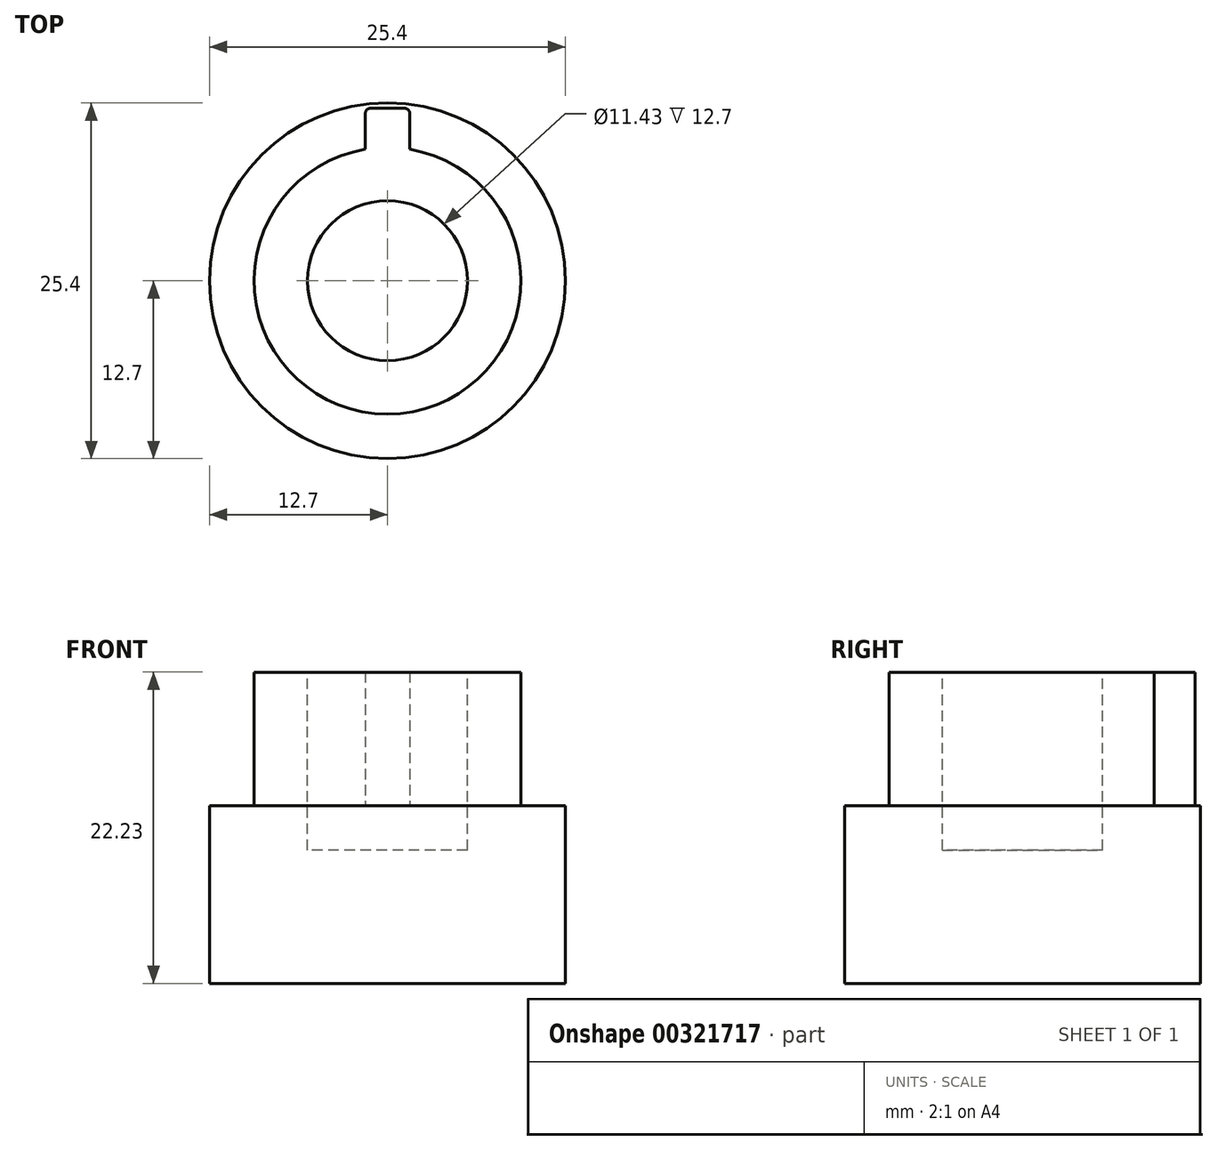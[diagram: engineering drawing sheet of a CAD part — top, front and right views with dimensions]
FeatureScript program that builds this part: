
annotation { "Feature Type Name" : "Feature", "Feature Type Description" : "" }
export const myFeature = defineFeature(function(context is Context, id is Id, definition is map)
    precondition{}
    {
        {
            var Q0;
            Q0=qCreatedBy(makeId("Top.planeOp"),FACE);
            var sketch = newSketch(context, id + "F0", { "sketchPlane" : qUnion([Q0])});
            skCircle(sketch, "E0", {"center": v(0, 0) * mm, "radius": 12.7 * mm});
            skSolve(sketch);
        }
        {
            var Q0;
            Q0=makeQuery(id+"F0.imprint","IMPRINT",FACE,{"disambiguationData":[TD([[makeQuery(id+"F0.imprint","IMPRINT",EDGE,{"derivedFrom":sQuery(id+"F0.wireOp",EDGE,"E0")}),1.0]])]});
            extrude(context, id + "F1", {"entities" : qUnion([Q0]), "depth" : 12.7 * mm});
        }
        {
            var Q0;
            Q0=makeQuery(id+"F1.opExtrude","CAP_FACE",FACE,{"disambiguationData":[OSD([sQuery(id+"F0.wireOp",EDGE,"E0")])],"isStart":false});
            var sketch = newSketch(context, id + "F2", { "sketchPlane" : qUnion([Q0])});
            skCircle(sketch, "E1", {"center": v(0, 0) * mm, "radius": 9.53 * mm});
            skSolve(sketch);
        }
        {
            var Q0;
            Q0=makeQuery(id+"F2.imprint","IMPRINT",FACE,{"disambiguationData":[TD([[makeQuery(id+"F2.imprint","IMPRINT",EDGE,{"derivedFrom":sQuery(id+"F2.wireOp",EDGE,"E1")}),1.0]])]});
            extrude(context, id + "F3", {"entities" : qUnion([Q0]), "operationType" : NewBodyOperationType.ADD, "depth" : 9.52 * mm});
        }
        {
            var Q0;
            Q0=makeQuery(id+"F3.opExtrude","CAP_FACE",FACE,{"disambiguationData":[OSD([sQuery(id+"F2.wireOp",EDGE,"E1")])],"isStart":false});
            var sketch = newSketch(context, id + "F4", { "sketchPlane" : qUnion([Q0])});
            skPoint(sketch, "E2", {"position": v(0, 9.53) * mm});
            skLineSegment(sketch, "E3.bottom", {"start": v(-1.59, 6.73) * mm, "end": v(1.59, 6.73) * mm});
            skLineSegment(sketch, "E3.top", {"start": v(-1.59, 12.32) * mm, "end": v(1.59, 12.32) * mm});
            skLineSegment(sketch, "E3.left", {"start": v(-1.59, 6.73) * mm, "end": v(-1.59, 12.32) * mm});
            skLineSegment(sketch, "E3.right", {"start": v(1.59, 6.73) * mm, "end": v(1.59, 12.32) * mm});
            skSolve(sketch);
        }
        {
            var Q0;
            {var subQ0=sQuery(id+"F4.wireOp",EDGE,"E3.bottom");Q0=makeQuery(id+"F4.imprint","IMPRINT",FACE,{"disambiguationData":[TD([[makeQuery(id+"F4.imprint","IMPRINT",EDGE,{"derivedFrom":subQ0}),1.0]])]});}
            var Q1;
            {var subQ0=sQuery(id+"F4.wireOp",EDGE,"E3.top");Q1=makeQuery(id+"F4.imprint","IMPRINT",FACE,{"disambiguationData":[TD([[makeQuery(id+"F4.imprint","IMPRINT",EDGE,{"derivedFrom":subQ0}),-1.0]])]});}
            extrude(context, id + "F5", {"entities" : qUnion([Q0, Q1]), "operationType" : NewBodyOperationType.ADD, "oppositeDirection" : true, "depth" : 10.16 * mm});
        }
        {
            var Q0;
            Q0=makeQuery(id+"F3.opExtrude","CAP_FACE",FACE,{"disambiguationData":[OSD([sQuery(id+"F2.wireOp",EDGE,"E1")])],"isStart":false});
            var sketch = newSketch(context, id + "F6", { "sketchPlane" : qUnion([Q0])});
            skCircle(sketch, "E4", {"center": v(0, 0) * mm, "radius": 5.72 * mm});
            skSolve(sketch);
        }
        {
            var Q0;
            Q0=makeQuery(id+"F6.imprint","IMPRINT",FACE,{"disambiguationData":[TD([[makeQuery(id+"F6.imprint","IMPRINT",EDGE,{"derivedFrom":sQuery(id+"F6.wireOp",EDGE,"E4")}),1.0]])]});
            extrude(context, id + "F7", {"entities" : qUnion([Q0]), "operationType" : NewBodyOperationType.REMOVE, "oppositeDirection" : true, "depth" : 12.7 * mm});
        }
        {
            var Q0;
            Q0=makeQuery(id+"F5.opExtrude","SWEPT_EDGE",EDGE,{"disambiguationData":[OSD([sQuery(id+"F4.wireOp",EDGE,"E3.top"),sQuery(id+"F4.wireOp",EDGE,"E3.right")])]});
            var Q1;
            Q1=makeQuery(id+"F5.opExtrude","SWEPT_EDGE",EDGE,{"disambiguationData":[OSD([sQuery(id+"F4.wireOp",EDGE,"E3.top"),sQuery(id+"F4.wireOp",EDGE,"E3.left")])]});
            fillet(context, id + "F8", {"entities" : qUnion([Q0, Q1]), "radius" : 0.38 * mm, "tangentPropagation" : true, "allowEdgeOverflow" : false});
        }
    });
